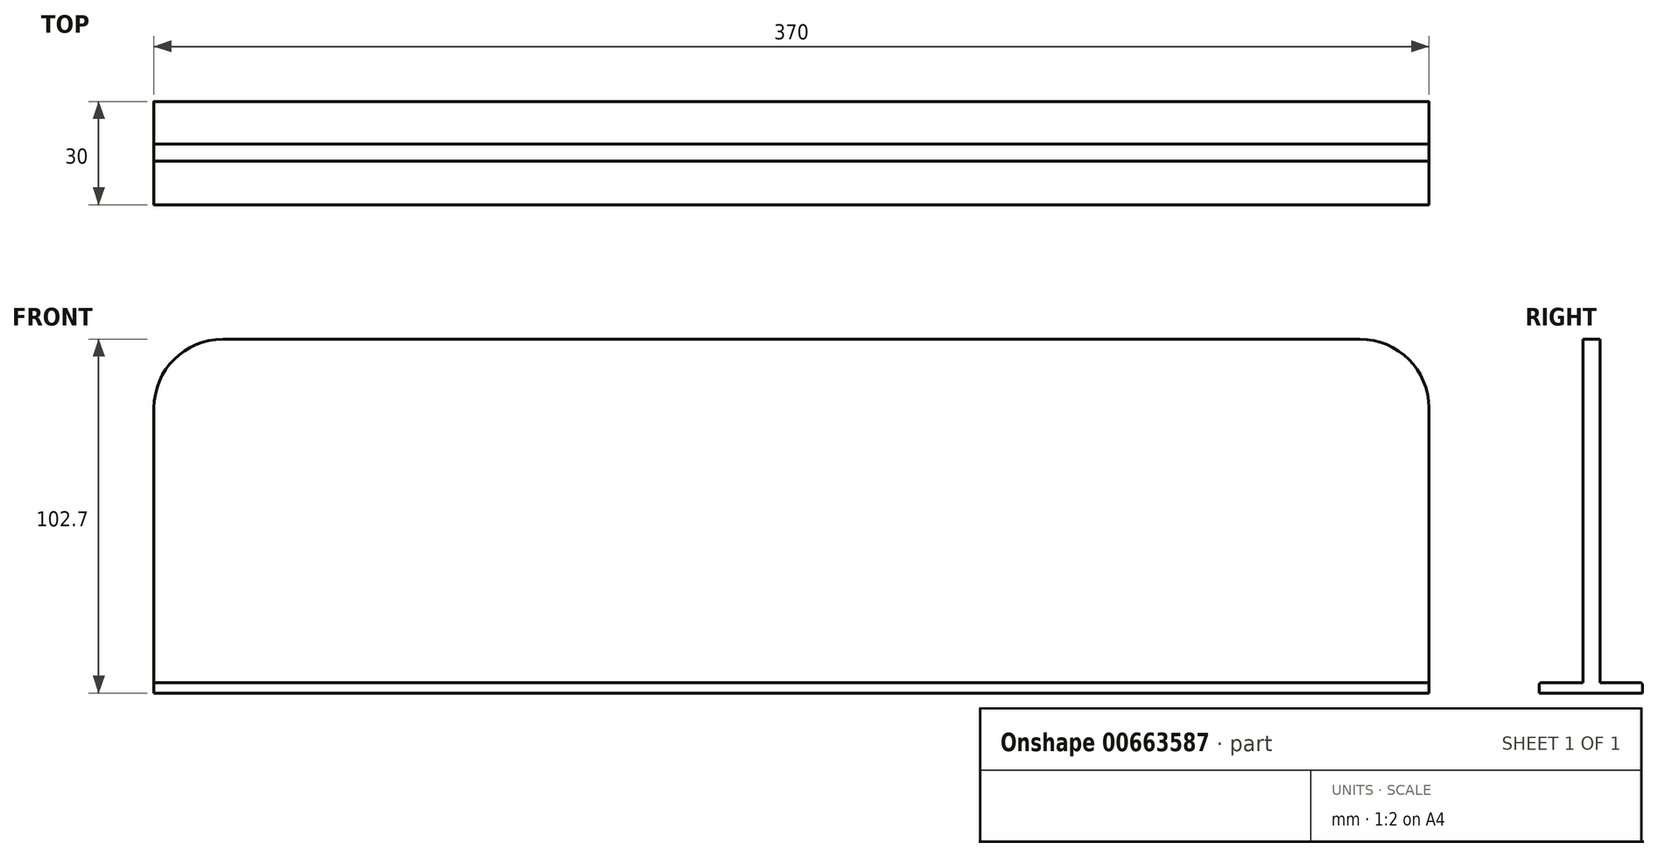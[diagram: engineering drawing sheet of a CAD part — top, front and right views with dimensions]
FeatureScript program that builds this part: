
annotation { "Feature Type Name" : "Feature", "Feature Type Description" : "" }
export const myFeature = defineFeature(function(context is Context, id is Id, definition is map)
    precondition{}
    {
        {
            var Q0;
            Q0=qCreatedBy(makeId("Front.planeOp"),FACE);
            var sketch = newSketch(context, id + "F0", { "sketchPlane" : qUnion([Q0])});
            skLineSegment(sketch, "E0.bottom", {"start": v(165, 50) * mm, "end": v(-165, 50) * mm});
            skLineSegment(sketch, "E0.top", {"start": v(185, -50) * mm, "end": v(-185, -50) * mm});
            skLineSegment(sketch, "E0.left", {"start": v(185, 30) * mm, "end": v(185, -50) * mm});
            skLineSegment(sketch, "E0.right", {"start": v(-185, 30) * mm, "end": v(-185, -50) * mm});
            skPoint(sketch, "E0.middle", {"position": v(0, 0) * mm});
            skPoint(sketch, "E1.visualSharp", {"position": v(-185, 50) * mm});
            skArc(sketch, "E1.filletArc", {"start": v(-175, 50) * mm, "mid": v(-182.07, 47.07) * mm, "end": v(-185, 40) * mm});
            skPoint(sketch, "E2.visualSharp", {"position": v(185, 50) * mm});
            skArc(sketch, "E2.filletArc", {"start": v(185, 30) * mm, "mid": v(179.14, 44.14) * mm, "end": v(165, 50) * mm});
            skArc(sketch, "E3.filletArc", {"start": v(-165, 50) * mm, "mid": v(-179.14, 44.14) * mm, "end": v(-185, 30) * mm});
            skSolve(sketch);
        }
        {
            var Q0;
            Q0=makeQuery(id+"F0.imprint","IMPRINT",FACE,{"disambiguationData":[TD([[makeQuery(id+"F0.imprint","IMPRINT",EDGE,{"derivedFrom":sQuery(id+"F0.wireOp",EDGE,"E0.bottom")}),1.0]])]});
            extrude(context, id + "F1", {"entities" : qUnion([Q0]), "depth" : 5 * mm, "offsetDistance" : 25 * mm});
        }
        {
            var Q0;
            Q0=qCreatedBy(makeId("Right.planeOp"),FACE);
            var sketch = newSketch(context, id + "F2", { "sketchPlane" : qUnion([Q0])});
            skLineSegment(sketch, "E4", {"start": v(11.66, -49.7) * mm, "end": v(-16.98, -49.7) * mm});
            skLineSegment(sketch, "E5", {"start": v(-17.66, -50.38) * mm, "end": v(-17.66, -52.7) * mm});
            skLineSegment(sketch, "E6", {"start": v(-17.66, -52.7) * mm, "end": v(12.34, -52.7) * mm});
            skLineSegment(sketch, "E7", {"start": v(12.34, -52.7) * mm, "end": v(12.34, -50.38) * mm});
            skPoint(sketch, "E8.visualSharp", {"position": v(-17.66, -49.7) * mm});
            skArc(sketch, "E8.filletArc", {"start": v(-16.98, -49.7) * mm, "mid": v(-17.46, -49.9) * mm, "end": v(-17.66, -50.38) * mm});
            skPoint(sketch, "E9.visualSharp", {"position": v(12.34, -49.7) * mm});
            skArc(sketch, "E9.filletArc", {"start": v(12.34, -50.38) * mm, "mid": v(12.14, -49.9) * mm, "end": v(11.66, -49.7) * mm});
            skSolve(sketch);
        }
        {
            var Q0;
            Q0=makeQuery(id+"F2.imprint","IMPRINT",FACE,{"disambiguationData":[TD([[makeQuery(id+"F2.imprint","IMPRINT",EDGE,{"derivedFrom":sQuery(id+"F2.wireOp",EDGE,"E4")}),1.0]])]});
            extrude(context, id + "F3", {"entities" : qUnion([Q0]), "operationType" : NewBodyOperationType.ADD, "depth" : 370 * mm, "offsetDistance" : 25 * mm, "symmetric" : true});
        }
    });
